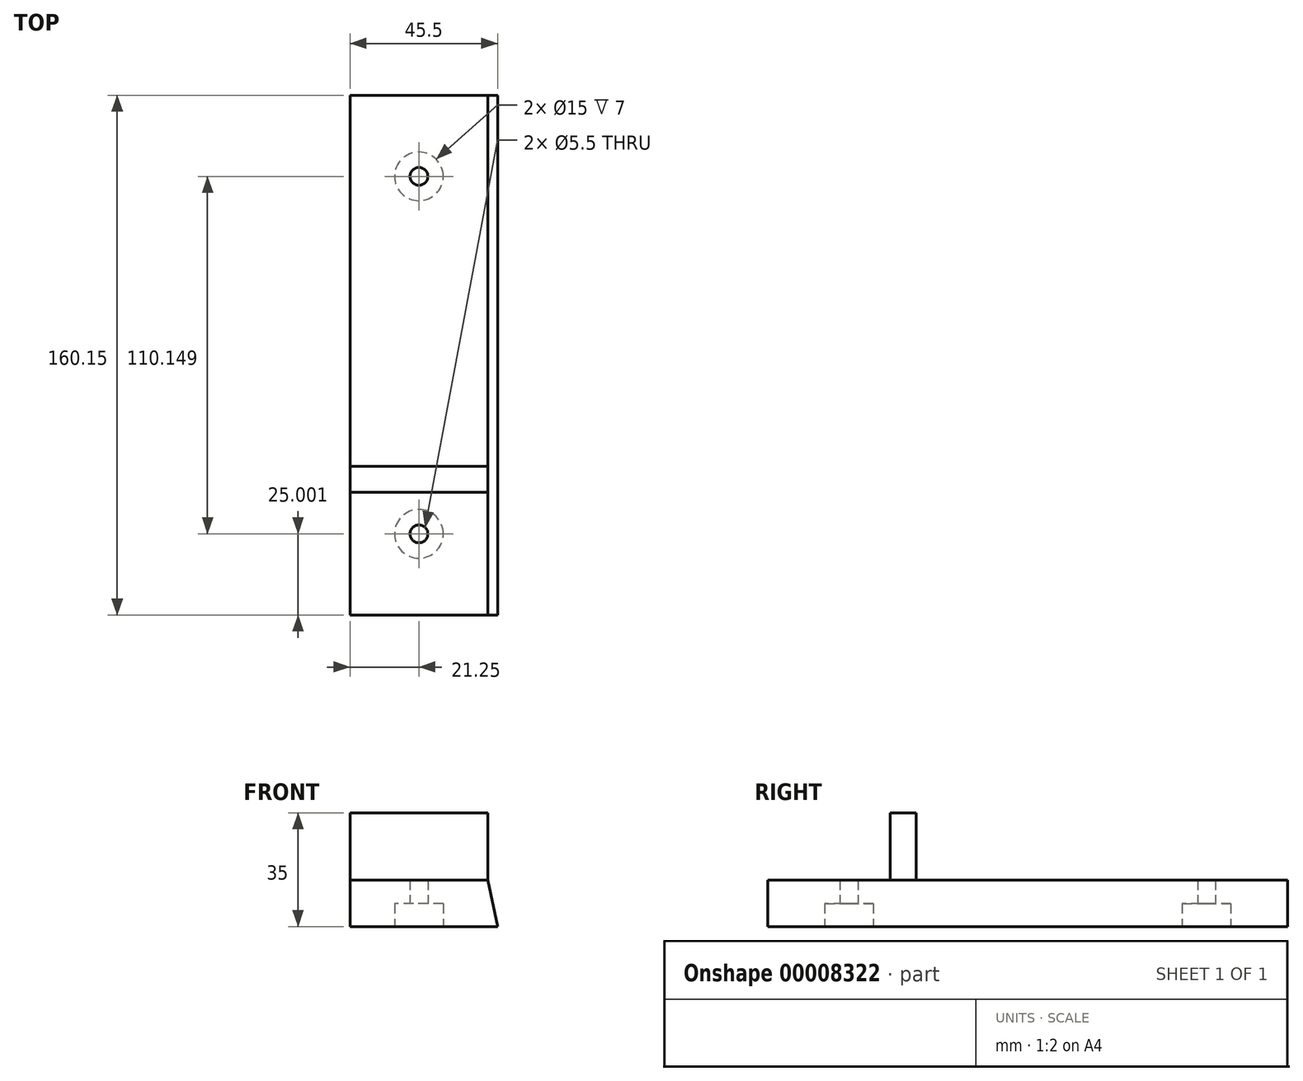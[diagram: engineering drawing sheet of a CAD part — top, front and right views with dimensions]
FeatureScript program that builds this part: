
annotation { "Feature Type Name" : "Feature", "Feature Type Description" : "" }
export const myFeature = defineFeature(function(context is Context, id is Id, definition is map)
    precondition{}
    {
        {
            var Q0;
            Q0=qCreatedBy(makeId("Front.planeOp"),FACE);
            var sketch = newSketch(context, id + "F0", { "sketchPlane" : qUnion([Q0])});
            skLineSegment(sketch, "E0", {"start": v(0, 0) * mm, "end": v(45.5, 0) * mm});
            skLineSegment(sketch, "E1", {"start": v(45.5, 0) * mm, "end": v(42.5, 14.28) * mm});
            skLineSegment(sketch, "E2", {"start": v(42.5, 14.28) * mm, "end": v(0, 14.28) * mm});
            skLineSegment(sketch, "E3", {"start": v(0, 14.28) * mm, "end": v(0, 0) * mm});
            skSolve(sketch);
        }
        {
            var Q0;
            Q0=makeQuery(id+"F0.imprint","IMPRINT",FACE,{"disambiguationData":[TD([[makeQuery(id+"F0.imprint","IMPRINT",EDGE,{"derivedFrom":sQuery(id+"F0.wireOp",EDGE,"E0")}),1.0]])]});
            extrude(context, id + "F1", {"entities" : qUnion([Q0]), "depth" : 160.15 * mm});
        }
        {
            var Q0;
            Q0=qCreatedBy(makeId("Top.planeOp"),FACE);
            var sketch = newSketch(context, id + "F2", { "sketchPlane" : qUnion([Q0])});
            skCircle(sketch, "E4", {"center": v(21.25, -25) * mm, "radius": 2.75 * mm});
            skCircle(sketch, "E5", {"center": v(21.25, -135.15) * mm, "radius": 2.75 * mm});
            skCircle(sketch, "E6", {"center": v(21.25, -25) * mm, "radius": 7.5 * mm});
            skCircle(sketch, "E7", {"center": v(21.25, -135.15) * mm, "radius": 7.5 * mm});
            skSolve(sketch);
        }
        {
            var Q0;
            Q0=makeQuery(id+"F2.imprint","IMPRINT",FACE,{"disambiguationData":[TD([[makeQuery(id+"F2.imprint","IMPRINT",EDGE,{"derivedFrom":sQuery(id+"F2.wireOp",EDGE,"E5")}),1.0]])]});
            var Q1;
            Q1=makeQuery(id+"F2.imprint","IMPRINT",FACE,{"disambiguationData":[TD([[makeQuery(id+"F2.imprint","IMPRINT",EDGE,{"derivedFrom":sQuery(id+"F2.wireOp",EDGE,"E4")}),1.0]])]});
            extrude(context, id + "F3", {"entities" : qUnion([Q0, Q1]), "depth" : 22 * mm, "hasSecondDirection" : true, "secondDirectionOppositeDirection" : true, "secondDirectionDepth" : 7.48 * mm});
        }
        {
            var Q0;
            Q0=makeQuery(id+"F2.imprint","IMPRINT",FACE,{"disambiguationData":[TD([[makeQuery(id+"F2.imprint","IMPRINT",EDGE,{"derivedFrom":sQuery(id+"F2.wireOp",EDGE,"E5")}),-1.0]])]});
            var Q1;
            Q1=makeQuery(id+"F2.imprint","IMPRINT",FACE,{"disambiguationData":[TD([[makeQuery(id+"F2.imprint","IMPRINT",EDGE,{"derivedFrom":sQuery(id+"F2.wireOp",EDGE,"E4")}),-1.0]])]});
            extrude(context, id + "F4", {"entities" : qUnion([Q0, Q1]), "depth" : 7 * mm, "hasSecondDirection" : true, "secondDirectionOppositeDirection" : true, "secondDirectionDepth" : 4.28 * mm});
        }
        {
            var Q0;
            Q0=makeQuery(id+"F3.opExtrude","SWEPT_BODY",BODY,{"disambiguationData":[OSD([sQuery(id+"F2.wireOp",EDGE,"E5")])]});
            var Q1;
            Q1=makeQuery(id+"F3.opExtrude","SWEPT_BODY",BODY,{"disambiguationData":[OSD([sQuery(id+"F2.wireOp",EDGE,"E4")])]});
            var Q2;
            Q2=makeQuery(id+"F4.opExtrude","SWEPT_BODY",BODY,{"disambiguationData":[OSD([sQuery(id+"F2.wireOp",EDGE,"E5"),sQuery(id+"F2.wireOp",EDGE,"E7")])]});
            var Q3;
            Q3=makeQuery(id+"F4.opExtrude","SWEPT_BODY",BODY,{"disambiguationData":[OSD([sQuery(id+"F2.wireOp",EDGE,"E4"),sQuery(id+"F2.wireOp",EDGE,"E6")])]});
            var Q4;
            Q4=makeQuery(id+"F1.opExtrude","SWEPT_BODY",BODY,{"disambiguationData":[OSD([sQuery(id+"F0.wireOp",EDGE,"E0"),sQuery(id+"F0.wireOp",EDGE,"E1"),sQuery(id+"F0.wireOp",EDGE,"E2"),sQuery(id+"F0.wireOp",EDGE,"E3")])]});
            booleanBodies(context, id + "F5", {"operationType" : BooleanOperationType.SUBTRACTION, "tools" : qUnion([Q0, Q1, Q2, Q3]), "targets" : qUnion([Q4])});
        }
        {
            var Q0;
            Q0=qCreatedBy(makeId("Top.planeOp"),FACE);
            var sketch = newSketch(context, id + "F6", { "sketchPlane" : qUnion([Q0])});
            skLineSegment(sketch, "E8.bottom", {"start": v(0, -114.4) * mm, "end": v(42.5, -114.4) * mm});
            skLineSegment(sketch, "E8.top", {"start": v(0, -122.4) * mm, "end": v(42.5, -122.4) * mm});
            skLineSegment(sketch, "E8.left", {"start": v(0, -114.4) * mm, "end": v(0, -122.4) * mm});
            skLineSegment(sketch, "E8.right", {"start": v(42.5, -114.4) * mm, "end": v(42.5, -122.4) * mm});
            skSolve(sketch);
        }
        {
            var Q0;
            Q0=makeQuery(id+"F6.imprint","IMPRINT",FACE,{"disambiguationData":[TD([[makeQuery(id+"F6.imprint","IMPRINT",EDGE,{"derivedFrom":sQuery(id+"F6.wireOp",EDGE,"E8.bottom")}),-1.0]])]});
            extrude(context, id + "F7", {"entities" : qUnion([Q0]), "operationType" : NewBodyOperationType.ADD, "depth" : 35 * mm});
        }
    });
